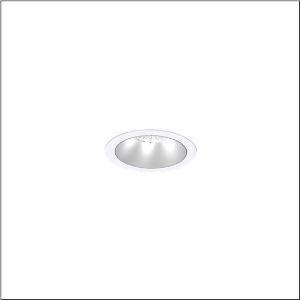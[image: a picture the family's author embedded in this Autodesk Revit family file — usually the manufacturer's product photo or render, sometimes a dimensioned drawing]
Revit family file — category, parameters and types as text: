
# Revit family: lunis_21_m_51db19ec91c
name_source: partatom
category: Lighting Fixtures
units: mm (PartAtom-declared; Revit-internal decimal feet)

## family parameters
Cut with Voids When Loaded = No
Host = Face
Light Source = No
Part Type = Normal
Room Calculation Point = No
Round Connector Dimension = Use Diameter
Shared = No

## types (1)
- --- (1 x LED, 3750 lm, 25.5 W, 4000K)
    Apparent Load = 26 VA
    CIE Flux Codes = 95 100 100 100 100
    Color Rendering = 80
    Color Temperature = 4000K
    Default Elevation = 1800 mm
    Description = Lunis 21,  M, downlight, light control with lens, of PMMA, anti glare with reflector, of PC, matt, light emission: direct distribution, LED rated luminous flux: 1.730lm, light colour: 830/840/865, with terminal, 5-pole, mains connection: 220..240V, AC/DC, 0/50..60Hz, housing, round, of diecast aluminium, traffic white (RAL 9016), diameter: 115mm, clamping range: 1..40mm, protection rating (complete): IP20, protection rating (on room side): IP54, insulation class (complete): insulation class II (safety insulation), certification: CE, impact resistance: IK03, packaging unit: 1 piece
    Height = 0 mm  [stored 0 ft]
    Lamp = 1 x LED
    Lamp Light Flux = 3750 lm
    Lamp Power = 25.5 W
    Lamp count = 1
    Length = 115 mm
    Luminous efficacy = 147 lm/W
    Manufacturer = Siteco
    ModVariant = No
    Model = 51DB19EC91C
    Mounting Place = Ceiling
    Mounting Type = Recessed
    Number of Poles = 1
    OnlyDefault = Yes
    Power Factor = 1
    Product Name = Lunis 21 M
    Product group = downlight
    ProductGroupID = 401
    Protection Class = Protection class II
    Protection Degree = IP 20
    RLX_Detail_Level = 1
    RLX_Emergency_Light_Flux = 0 lm
    RLX_Emergency_Type = 0
    RLX_Emergency_Type_DB = No
    RlxData = <blob elided: 11397 chars, md5=290dabf8>
    Socket = socket
    Standby Power = 0 W
    System Light Flux = 3750 lm
    System Power = 26 W
    Type Comments = individual setting: colour temperature 4000K, luminous flux: 100 % | (ON | ON | OFF | OFF) | 700 mA
    Type Image = l_1290856.jpg
    URL = http://relux.com
    VarID = @adj_026103
    Voltage = 0 V
    Weight = 0.00 kg
    Width = 0 mm  [stored 0 ft]

note: [stored X ft] marks values corroborated as IEEE doubles in the binary element streams (Revit-internal decimal feet)

## geometry (parser evidence)
native form markers: Sweep x8
no freeform markers — native parametric forms only
